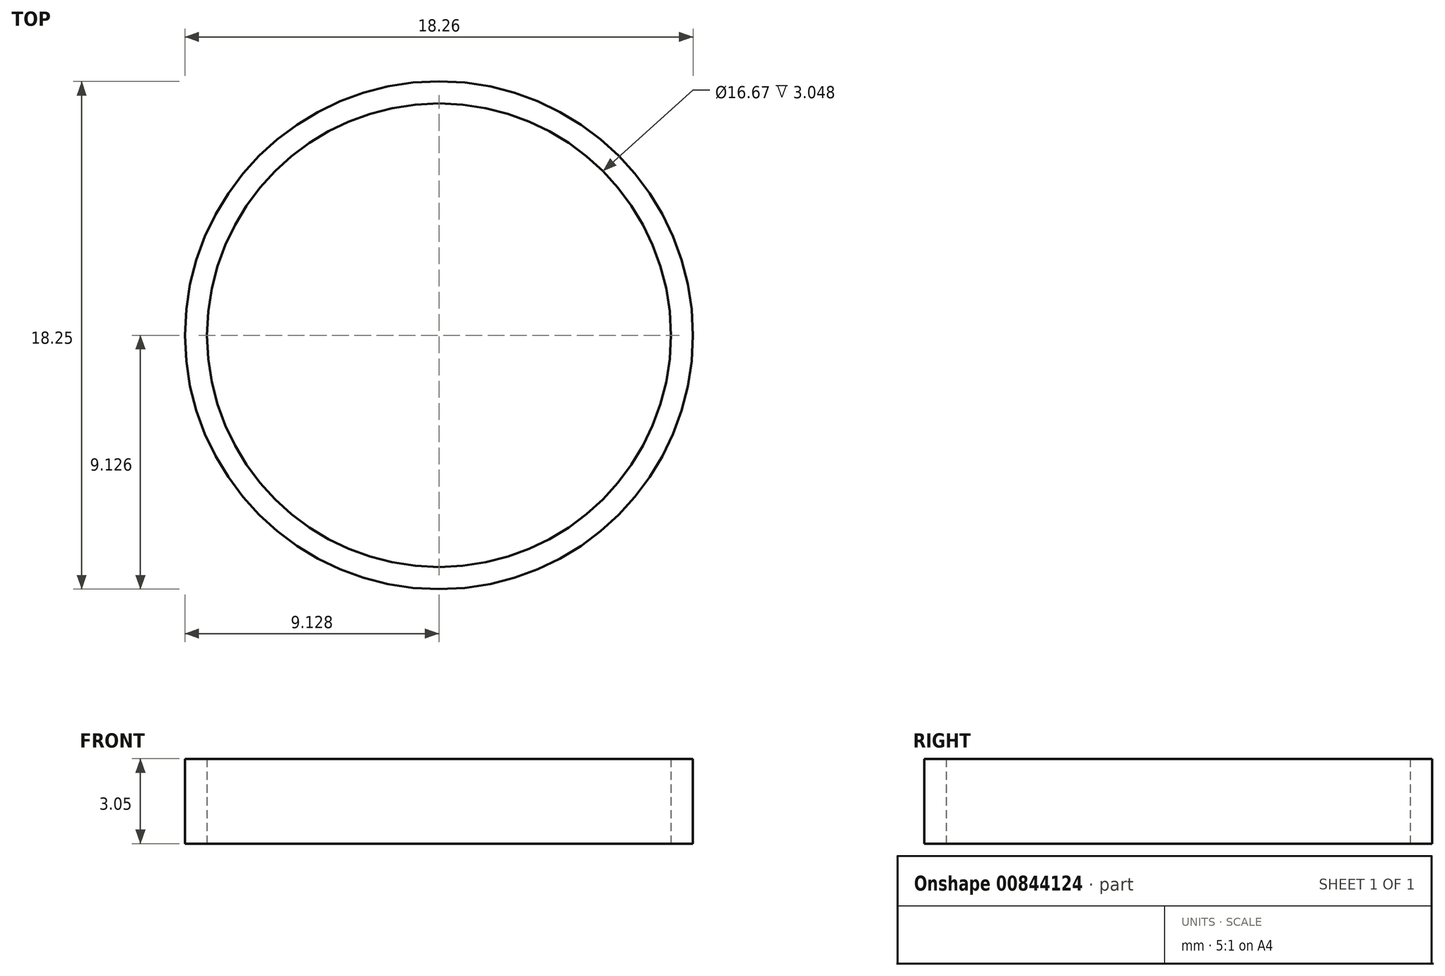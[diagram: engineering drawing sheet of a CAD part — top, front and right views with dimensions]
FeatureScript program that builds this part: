
annotation { "Feature Type Name" : "Feature", "Feature Type Description" : "" }
export const myFeature = defineFeature(function(context is Context, id is Id, definition is map)
    precondition{}
    {
        {
            var Q0;
            Q0=qCreatedBy(makeId("Top.planeOp"),FACE);
            var sketch = newSketch(context, id + "F0", { "sketchPlane" : qUnion([Q0])});
            skCircle(sketch, "E0", {"center": v(-36.64, 24.56) * mm, "radius": 8.33 * mm});
            skCircle(sketch, "E1", {"center": v(-36.64, 24.56) * mm, "radius": 9.13 * mm});
            skSolve(sketch);
        }
        {
            var Q0;
            Q0=makeQuery(id+"F0.imprint","IMPRINT",FACE,{"disambiguationData":[TD([[makeQuery(id+"F0.imprint","IMPRINT",EDGE,{"derivedFrom":sQuery(id+"F0.wireOp",EDGE,"E0")}),-1.0]])]});
            extrude(context, id + "F1", {"entities" : qUnion([Q0]), "depth" : 3.05 * mm, "offsetDistance" : 25.4 * mm});
        }
    });
